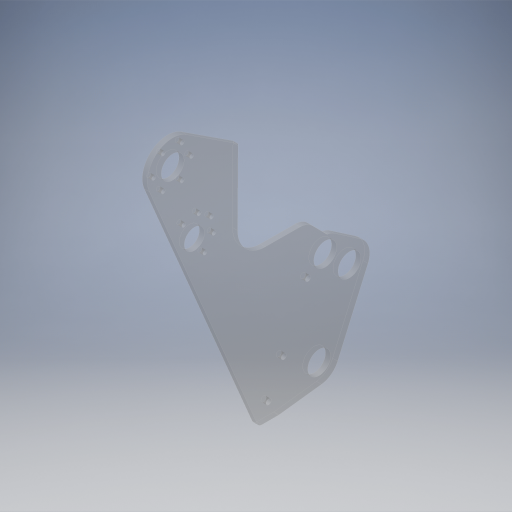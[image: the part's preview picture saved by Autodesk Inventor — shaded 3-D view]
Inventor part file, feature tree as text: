
AUTODESK INVENTOR PART (.ipt)
format: ipt  version: 2024.2 (Build 282272000, 272)  size: 504,832 bytes
history: native  units: in
note: dims shown in document units (in); Inventor stores cm internally (conversion verified against a paired STEP export)
features: sketch x10, extrude x10, projected_geometry x3, chamfer x1, fillet x1, other x1
ambient origin geometry x8: Origin, YZ Plane, XZ Plane, XY Plane, X Axis, Y Axis, Z Axis, Center Point
bodies: Solid1 (feature_tree)
feature tree (26):
  sketch  "Sketch1"  dims[d0=1.875in d2=0.1969in]
  extrude  "Extrusion1"  Depth=0.1969in
  extrude  "Extrusion2"  Depth=1.0in TaperAngle=0.0deg
  extrude  "Extrusion3"  Depth=1.0in TaperAngle=0.0deg
  sketch  "Sketch4"  dims[d15=1.0in d16=0.0in d19=3.1496in d21=360.0deg]
  extrude  "Extrusion7"  Depth=1.0in TaperAngle=360.0deg
  extrude  "Extrusion8"  Depth=0.25in
  extrude  "Extrusion9"  Depth=0.25in TaperAngle=0.0deg
  sketch  "Sketch9"  dims[d32=0.25in d33=0.0in d34=0.25in d35=0.0in]
  sketch  "Sketch10"  dims[d36=0.25in d37=0.0in d38=0.975in d39=0.125in d40=45.0deg]
  extrude  "Extrusion10"  Depth=14.8479in
  extrude  "Extrusion11"  Depth=0.25in TaperAngle=0.0deg
  extrude  "Extrusion12"  Depth=0.25in TaperAngle=45.0deg
  chamfer  "Chamfer1"  Distance=1.9685in
  fillet  "Fillet1"  [1 undecoded]
  extrude  "Extrusion5"  [1 undecoded]
  sketch  "Sketch2"  dims[d3=0.3937in d4=0.0in d5=1.0in d6=0.0in]
  projected_geometry  "Projected Loop1"
  sketch  "Sketch3"  dims[d7=2.3622in d9=360.0deg d11=1.0in d12=0.0in]
  sketch  "Sketch6"  dims[d23=0.25in d24=0.0in d25=0.125in]
  projected_geometry  "Projected Loop2"
  sketch  "Sketch7"  dims[d26=0.25in d27=0.0in d28=0.25in d29=0.0in]
  projected_geometry  "Projected Loop3"
  sketch  "Sketch8"  dims[d30=11.4128in d31=14.8479in]
  sketch  "Sketch11"  dims[d41=0.875in d8=1.9685in]
  other  "Part 1"
note: 2 required parameter values undecoded (feature->parameter linkage not recoverable at this tier; creation-order binding heuristic only, values carry confidence <= 0.55)
